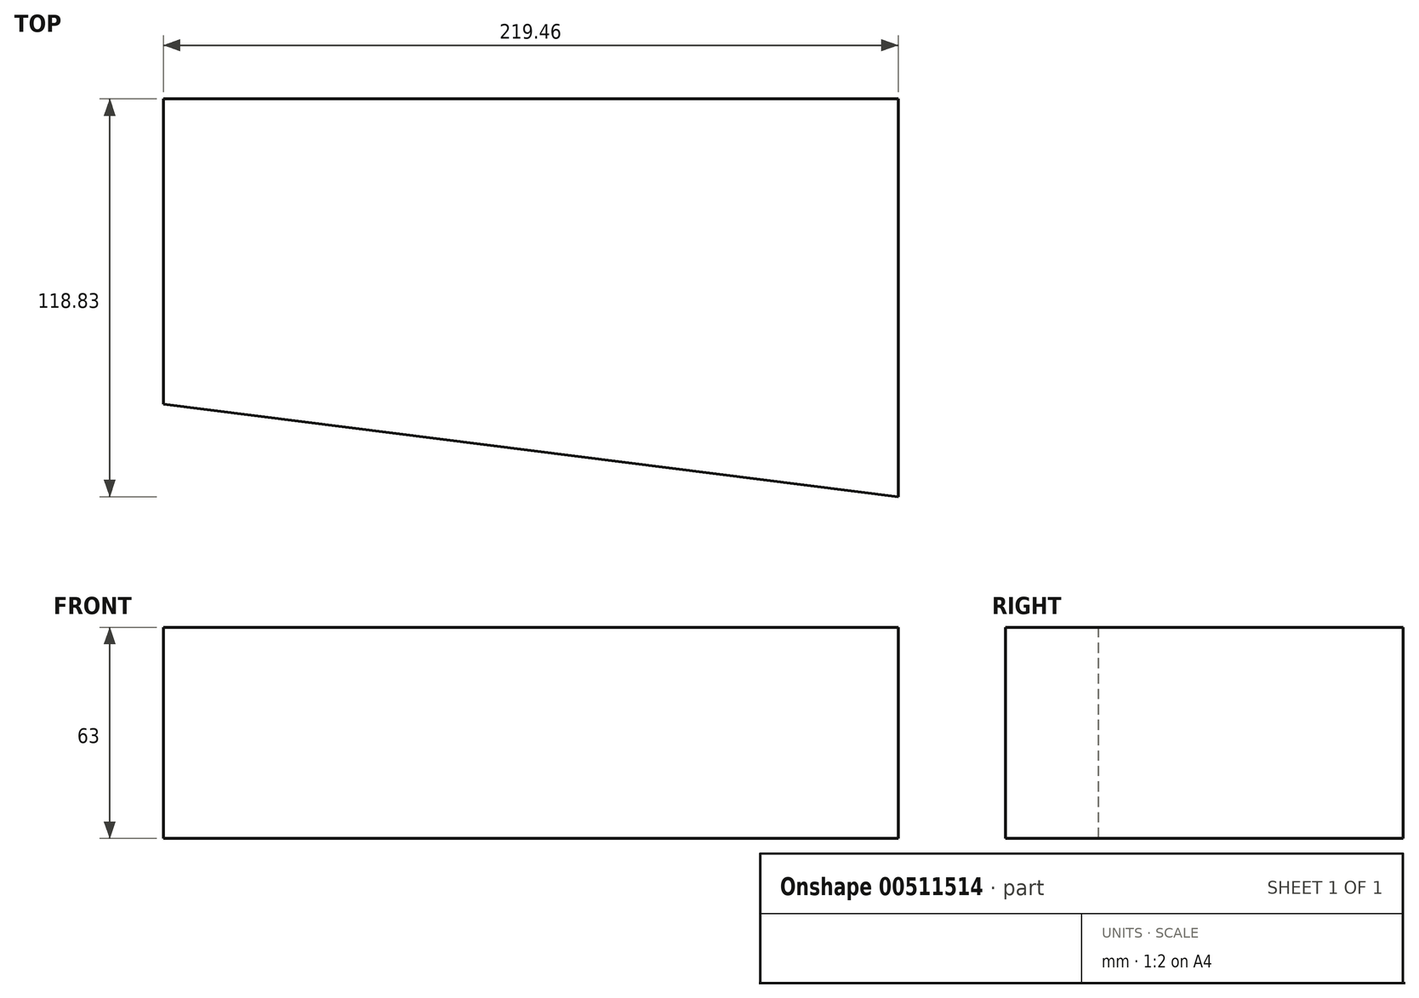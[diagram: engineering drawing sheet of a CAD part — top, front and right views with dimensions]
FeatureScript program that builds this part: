
annotation { "Feature Type Name" : "Feature", "Feature Type Description" : "" }
export const myFeature = defineFeature(function(context is Context, id is Id, definition is map)
    precondition{}
    {
        {
            var Q0;
            Q0=qCreatedBy(makeId("Top.planeOp"),FACE);
            var sketch = newSketch(context, id + "F0", { "sketchPlane" : qUnion([Q0])});
            skLineSegment(sketch, "E0", {"start": v(-124.08, -34.57) * mm, "end": v(-124.08, 56.57) * mm});
            skLineSegment(sketch, "E1", {"start": v(-124.08, 56.57) * mm, "end": v(95.38, 56.57) * mm});
            skLineSegment(sketch, "E2", {"start": v(95.38, 56.57) * mm, "end": v(95.38, -62.26) * mm});
            skLineSegment(sketch, "E3", {"start": v(95.38, -62.26) * mm, "end": v(-124.08, -34.57) * mm});
            skSolve(sketch);
        }
        {
            var Q0;
            Q0=makeQuery(id+"F0.imprint","IMPRINT",FACE,{"disambiguationData":[TD([[makeQuery(id+"F0.imprint","IMPRINT",EDGE,{"derivedFrom":sQuery(id+"F0.wireOp",EDGE,"E0")}),-1.0]])]});
            extrude(context, id + "F1", {"entities" : qUnion([Q0]), "depth" : 63 * mm});
        }
    });
